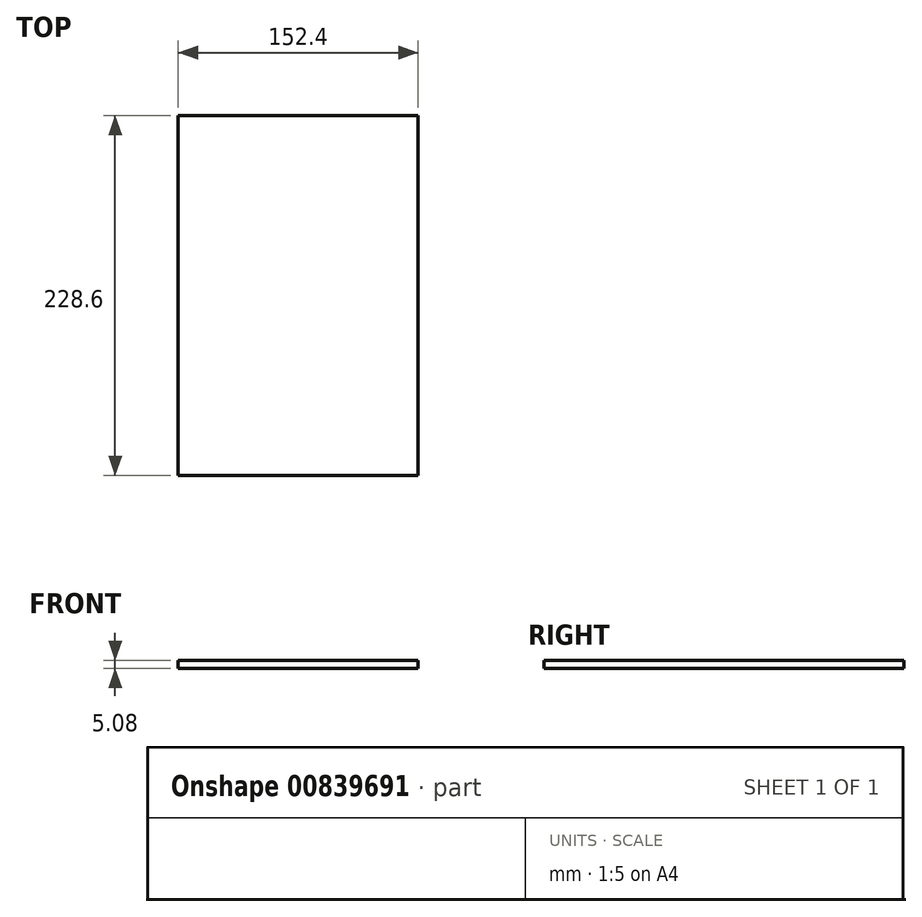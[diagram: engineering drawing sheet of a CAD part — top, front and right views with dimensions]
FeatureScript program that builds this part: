
annotation { "Feature Type Name" : "Feature", "Feature Type Description" : "" }
export const myFeature = defineFeature(function(context is Context, id is Id, definition is map)
    precondition{}
    {
        {
            var Q0;
            Q0=qCreatedBy(makeId("Top.planeOp"), FACE);
            var sketch = newSketch(context, id + "F0", { "sketchPlane" : qUnion([Q0])});
            skLineSegment(sketch, "E0.bottom", {"start": v(76.2, -114.3) * mm, "end": v(-76.2, -114.3) * mm});
            skLineSegment(sketch, "E0.top", {"start": v(76.2, 114.3) * mm, "end": v(-76.2, 114.3) * mm});
            skLineSegment(sketch, "E0.left", {"start": v(76.2, -114.3) * mm, "end": v(76.2, 114.3) * mm});
            skLineSegment(sketch, "E0.right", {"start": v(-76.2, -114.3) * mm, "end": v(-76.2, 114.3) * mm});
            skPoint(sketch, "E0.middle", {"position": v(0, 0) * mm});
            skSolve(sketch);
        }
        {
            var Q0;
            Q0 = qSketchRegion(id + "F0", true);
            extrude(context, id + "F1", {"entities" : qUnion([Q0]), "domain" : OperationDomain.MODEL, "flatOperationType" : FlatOperationType.REMOVE, "depth" : 5.08 * mm, "offsetDistance" : 25.4 * mm});
        }
    });
